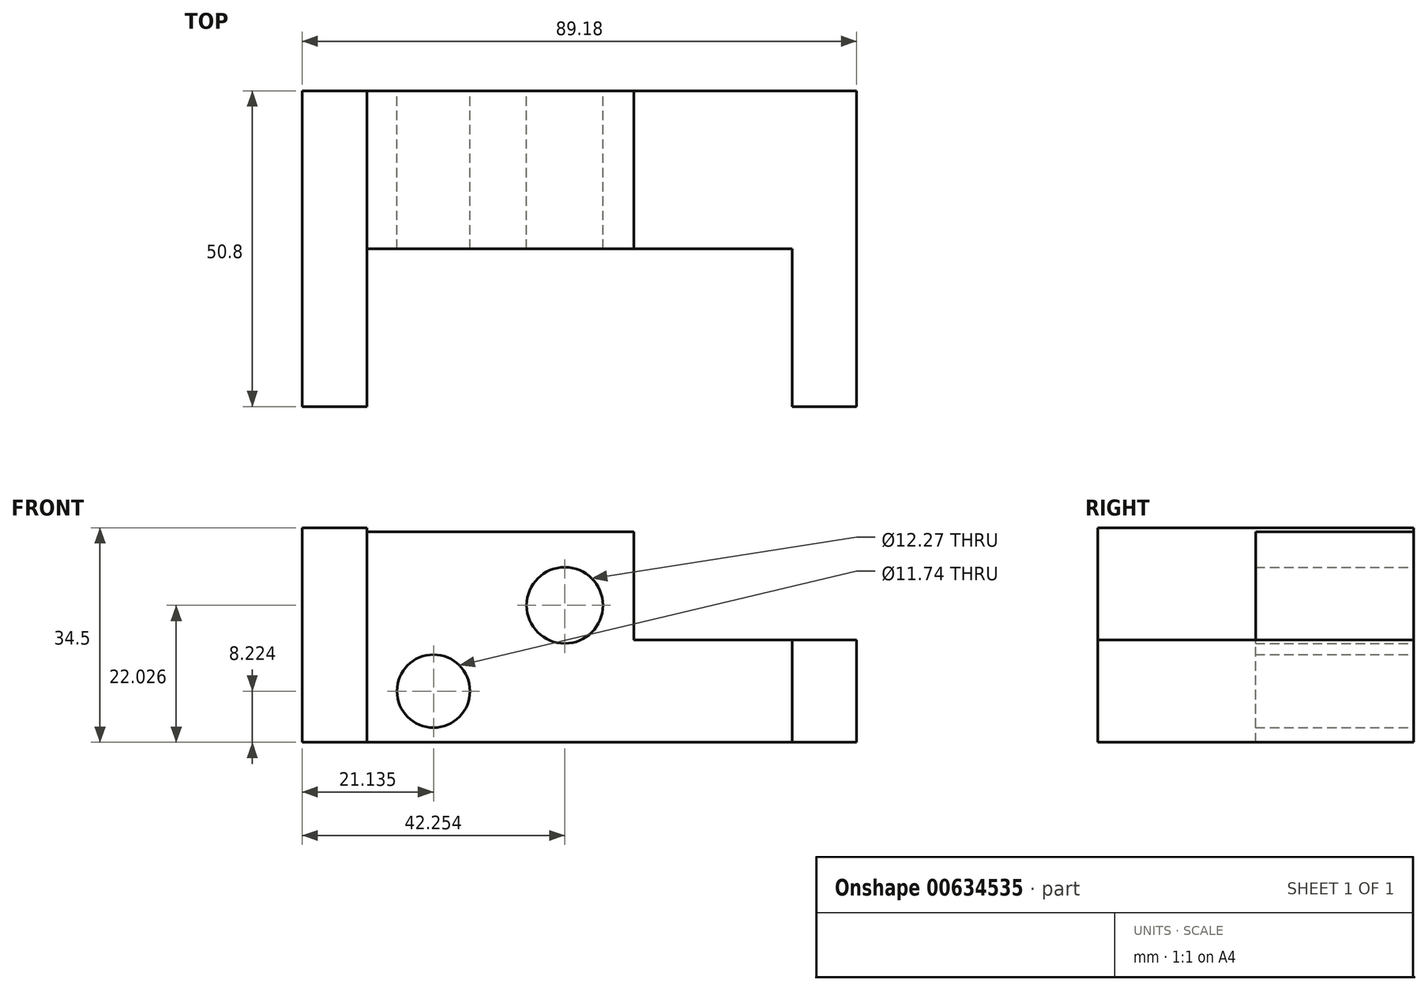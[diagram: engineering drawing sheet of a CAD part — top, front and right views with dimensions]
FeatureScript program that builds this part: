
annotation { "Feature Type Name" : "Feature", "Feature Type Description" : "" }
export const myFeature = defineFeature(function(context is Context, id is Id, definition is map)
    precondition{}
    {
        {
            var Q0;
            Q0=qCreatedBy(makeId("Front.planeOp"),FACE);
            var sketch = newSketch(context, id + "F0", { "sketchPlane" : qUnion([Q0])});
            skLineSegment(sketch, "E0.bottom", {"start": v(-48.07, 17.38) * mm, "end": v(-5.15, 17.38) * mm});
            skLineSegment(sketch, "E0.top", {"start": v(-48.07, -16.45) * mm, "end": v(-5.15, -16.45) * mm});
            skLineSegment(sketch, "E0.left", {"start": v(-48.07, 17.38) * mm, "end": v(-48.07, -16.45) * mm});
            skLineSegment(sketch, "E0.right", {"start": v(-5.15, 17.38) * mm, "end": v(-5.15, -16.45) * mm});
            skLineSegment(sketch, "E1.bottom", {"start": v(-5.15, -16.45) * mm, "end": v(20.28, -16.45) * mm});
            skLineSegment(sketch, "E1.top", {"start": v(-5.15, 0) * mm, "end": v(20.28, 0) * mm});
            skLineSegment(sketch, "E1.left", {"start": v(-5.15, -16.45) * mm, "end": v(-5.15, 0) * mm});
            skLineSegment(sketch, "E1.right", {"start": v(20.28, -16.45) * mm, "end": v(20.28, 0) * mm});
            skCircle(sketch, "E2", {"center": v(-37.4, -8.23) * mm, "radius": 5.87 * mm});
            skPoint(sketch, "E2.centerSnap0", {"position": v(-5.15, -8.23) * mm});
            skCircle(sketch, "E3", {"center": v(-16.28, 5.58) * mm, "radius": 6.14 * mm});
            skLineSegment(sketch, "E4.bottom", {"start": v(-48.07, -16.45) * mm, "end": v(-58.53, -16.45) * mm});
            skLineSegment(sketch, "E4.top", {"start": v(-48.07, 18.05) * mm, "end": v(-58.53, 18.05) * mm});
            skLineSegment(sketch, "E4.left", {"start": v(-48.07, -16.45) * mm, "end": v(-48.07, 18.05) * mm});
            skLineSegment(sketch, "E4.right", {"start": v(-58.53, -16.45) * mm, "end": v(-58.53, 18.05) * mm});
            skLineSegment(sketch, "E5.bottom", {"start": v(20.28, -16.45) * mm, "end": v(30.65, -16.45) * mm});
            skLineSegment(sketch, "E5.top", {"start": v(20.28, 0) * mm, "end": v(30.65, 0) * mm});
            skLineSegment(sketch, "E5.right", {"start": v(30.65, -16.45) * mm, "end": v(30.65, 0) * mm});
            skSolve(sketch);
        }
        {
            var Q0;
            Q0=makeQuery(id+"F0.imprint","IMPRINT",FACE,{"disambiguationData":[TD([[makeQuery(id+"F0.imprint","IMPRINT",EDGE,{"derivedFrom":sQuery(id+"F0.wireOp",EDGE,"E1.bottom")}),1.0]])]});
            var Q1;
            {var subQ1=sQuery(id+"F0.wireOp",EDGE,"E0.bottom");Q1=makeQuery(id+"F0.imprint","IMPRINT",FACE,{"disambiguationData":[TD([[makeQuery(id+"F0.imprint","IMPRINT",EDGE,{"derivedFrom":subQ1}),-1.0]])]});}
            extrude(context, id + "F1", {"entities" : qUnion([Q0, Q1]), "depth" : 25.4 * mm, "offsetDistance" : 25.4 * mm});
        }
        {
            var Q0;
            Q0=makeQuery(id+"F0.imprint","IMPRINT",FACE,{"disambiguationData":[TD([[makeQuery(id+"F0.imprint","IMPRINT",EDGE,{"derivedFrom":sQuery(id+"F0.wireOp",EDGE,"E5.bottom")}),1.0]])]});
            var Q1;
            {var subQ3=sQuery(id+"F0.wireOp",EDGE,"E4.bottom");Q1=makeQuery(id+"F0.imprint","IMPRINT",FACE,{"disambiguationData":[TD([[makeQuery(id+"F0.imprint","IMPRINT",EDGE,{"derivedFrom":subQ3}),-1.0]])]});}
            extrude(context, id + "F2", {"entities" : qUnion([Q0, Q1]), "operationType" : NewBodyOperationType.ADD, "depth" : 50.8 * mm, "offsetDistance" : 25.4 * mm});
        }
    });
